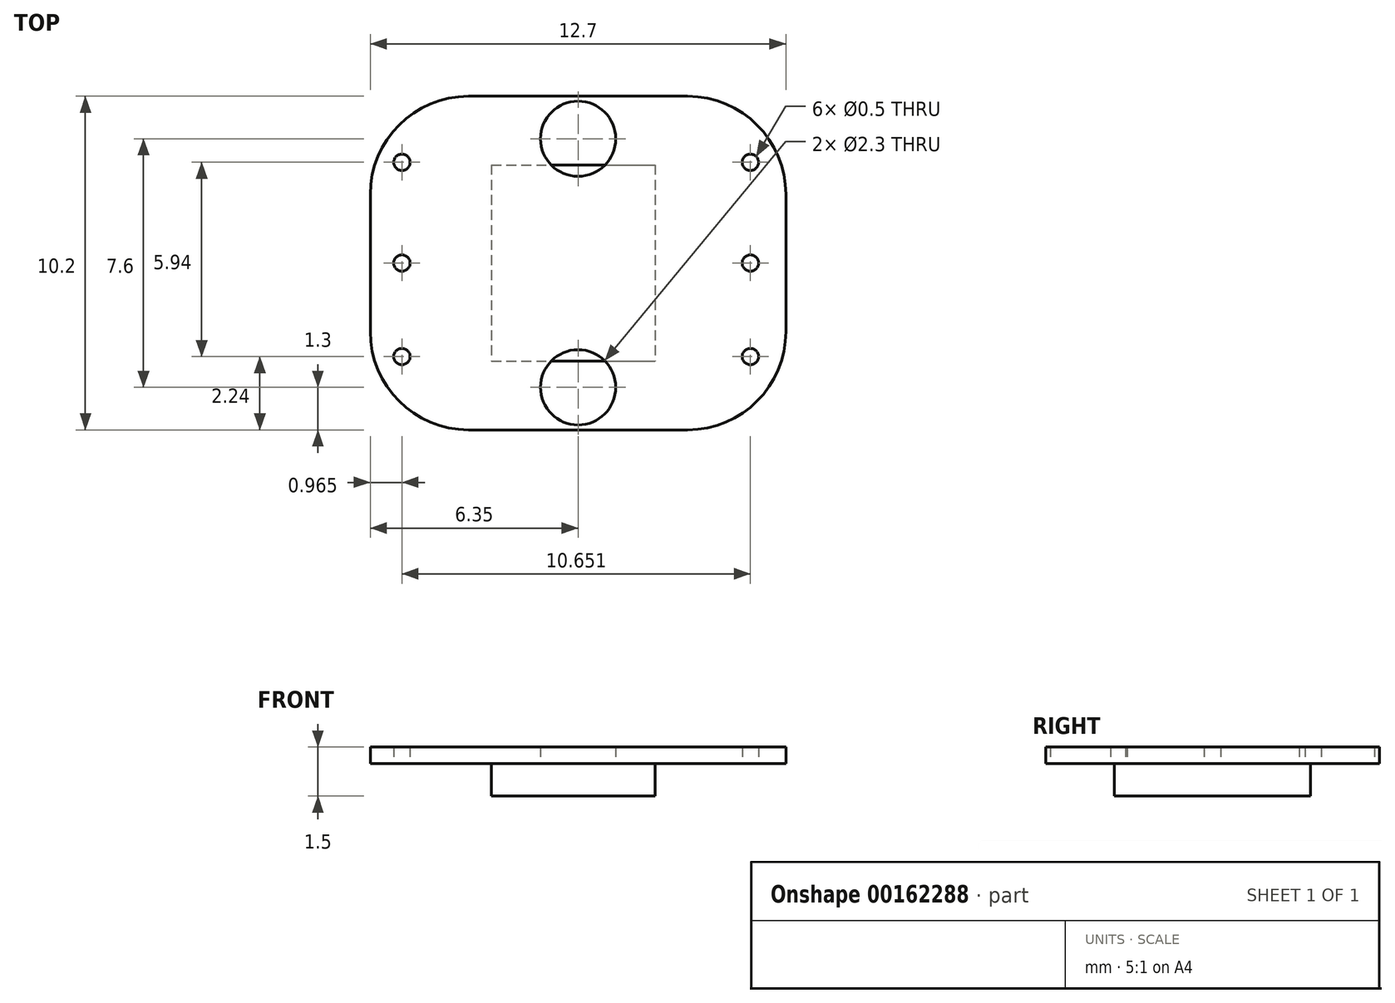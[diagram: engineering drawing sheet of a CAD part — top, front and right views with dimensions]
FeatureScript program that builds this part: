
annotation { "Feature Type Name" : "Feature", "Feature Type Description" : "" }
export const myFeature = defineFeature(function(context is Context, id is Id, definition is map)
    precondition{}
    {
        {
            var Q0;
            Q0=qCreatedBy(makeId("Top.planeOp"),FACE);
            var sketch = newSketch(context, id + "F0", { "sketchPlane" : qUnion([Q0])});
            skLineSegment(sketch, "E0.bottom", {"start": v(0, 10.2) * mm, "end": v(12.7, 10.2) * mm});
            skLineSegment(sketch, "E0.top", {"start": v(0, 0) * mm, "end": v(12.7, 0) * mm});
            skLineSegment(sketch, "E0.left", {"start": v(0, 10.2) * mm, "end": v(0, 0) * mm});
            skLineSegment(sketch, "E0.right", {"start": v(12.7, 10.2) * mm, "end": v(12.7, 0) * mm});
            skLineSegment(sketch, "E1.bottom", {"start": v(3.7, 8.1) * mm, "end": v(8.7, 8.1) * mm});
            skLineSegment(sketch, "E1.top", {"start": v(3.7, 2.1) * mm, "end": v(8.7, 2.1) * mm});
            skLineSegment(sketch, "E1.left", {"start": v(3.7, 8.1) * mm, "end": v(3.7, 2.1) * mm});
            skLineSegment(sketch, "E1.right", {"start": v(8.7, 8.1) * mm, "end": v(8.7, 2.1) * mm});
            skPoint(sketch, "E2", {"position": v(0.97, 5.1) * mm});
            skPoint(sketch, "E2.positionSnap0", {"position": v(0, 5.1) * mm});
            skPoint(sketch, "E3", {"position": v(0.97, 8.18) * mm});
            skPoint(sketch, "E4", {"position": v(0.97, 2.24) * mm});
            skPoint(sketch, "E5", {"position": v(11.62, 5.1) * mm});
            skPoint(sketch, "E5.positionSnap0", {"position": v(12.7, 5.1) * mm});
            skPoint(sketch, "E6", {"position": v(11.62, 8.18) * mm});
            skPoint(sketch, "E7", {"position": v(11.62, 2.24) * mm});
            skPoint(sketch, "E8", {"position": v(6.35, 8.9) * mm});
            skPoint(sketch, "E8.positionSnap0", {"position": v(6.35, 10.2) * mm});
            skPoint(sketch, "E9", {"position": v(6.35, 1.3) * mm});
            skPoint(sketch, "E9.positionSnap0", {"position": v(6.35, 0) * mm});
            skSolve(sketch);
        }
        {
            var Q0;
            Q0=makeQuery(id+"F0.imprint","IMPRINT",FACE,{"disambiguationData":[TD([[makeQuery(id+"F0.imprint","IMPRINT",EDGE,{"derivedFrom":sQuery(id+"F0.wireOp",EDGE,"E0.bottom")}),-1.0]])]});
            var Q1;
            Q1=makeQuery(id+"F0.imprint","IMPRINT",FACE,{"disambiguationData":[TD([[makeQuery(id+"F0.imprint","IMPRINT",EDGE,{"derivedFrom":sQuery(id+"F0.wireOp",EDGE,"E1.bottom")}),-1.0]])]});
            extrude(context, id + "F1", {"entities" : qUnion([Q0, Q1]), "depth" : 0.5 * mm});
        }
        {
            var Q0;
            Q0=makeQuery(id+"F0.imprint","IMPRINT",FACE,{"disambiguationData":[TD([[makeQuery(id+"F0.imprint","IMPRINT",EDGE,{"derivedFrom":sQuery(id+"F0.wireOp",EDGE,"E1.bottom")}),-1.0]])]});
            extrude(context, id + "F2", {"entities" : qUnion([Q0]), "oppositeDirection" : true, "depth" : 1 * mm});
        }
        {
            var Q0;
            Q0=sQuery(id+"F0.wireOp",VERTEX,"E7");
            var Q1;
            Q1=sQuery(id+"F0.wireOp",VERTEX,"E5");
            var Q2;
            Q2=sQuery(id+"F0.wireOp",VERTEX,"E6");
            var Q3;
            Q3=sQuery(id+"F0.wireOp",VERTEX,"E3");
            var Q4;
            Q4=sQuery(id+"F0.wireOp",VERTEX,"E2");
            var Q5;
            Q5=sQuery(id+"F0.wireOp",VERTEX,"E4");
            var Q6;
            Q6=makeQuery(id+"F1.opExtrude","SWEPT_BODY",BODY,{"disambiguationData":[OSD([sQuery(id+"F0.wireOp",EDGE,"E0.bottom"),sQuery(id+"F0.wireOp",EDGE,"E0.top"),sQuery(id+"F0.wireOp",EDGE,"E0.left"),sQuery(id+"F0.wireOp",EDGE,"E0.right")])]});
            hole(context, id + "F3", {"style" : HoleStyle.SIMPLE, "endStyle" : HoleEndStyle.THROUGH, "oppositeDirection" : true, "holeDiameter" : 0.5 * mm, "startFromSketch" : true, "locations" : qUnion([Q0, Q1, Q2, Q3, Q4, Q5]), "scope" : qUnion([Q6]), "isTappedThrough" : true});
        }
        {
            var Q0;
            Q0=sQuery(id+"F0.wireOp",VERTEX,"E9");
            var Q1;
            Q1=sQuery(id+"F0.wireOp",VERTEX,"E8");
            var Q2;
            Q2=makeQuery(id+"F1.opExtrude","SWEPT_BODY",BODY,{"disambiguationData":[OSD([sQuery(id+"F0.wireOp",EDGE,"E0.bottom"),sQuery(id+"F0.wireOp",EDGE,"E0.top"),sQuery(id+"F0.wireOp",EDGE,"E0.left"),sQuery(id+"F0.wireOp",EDGE,"E0.right")])]});
            hole(context, id + "F4", {"style" : HoleStyle.SIMPLE, "endStyle" : HoleEndStyle.THROUGH, "oppositeDirection" : true, "holeDiameter" : 2.3 * mm, "startFromSketch" : true, "locations" : qUnion([Q0, Q1]), "scope" : qUnion([Q2]), "isTappedThrough" : true});
        }
        {
            var Q0;
            Q0=makeQuery(id+"F1.opExtrude","SWEPT_EDGE",EDGE,{"disambiguationData":[OSD([sQuery(id+"F0.wireOp",EDGE,"E0.bottom"),sQuery(id+"F0.wireOp",EDGE,"E0.left")])]});
            var Q1;
            Q1=makeQuery(id+"F1.opExtrude","SWEPT_EDGE",EDGE,{"disambiguationData":[OSD([sQuery(id+"F0.wireOp",EDGE,"E0.bottom"),sQuery(id+"F0.wireOp",EDGE,"E0.right")])]});
            var Q2;
            Q2=makeQuery(id+"F1.opExtrude","SWEPT_EDGE",EDGE,{"disambiguationData":[OSD([sQuery(id+"F0.wireOp",EDGE,"E0.top"),sQuery(id+"F0.wireOp",EDGE,"E0.left")])]});
            var Q3;
            Q3=makeQuery(id+"F1.opExtrude","SWEPT_EDGE",EDGE,{"disambiguationData":[OSD([sQuery(id+"F0.wireOp",EDGE,"E0.top"),sQuery(id+"F0.wireOp",EDGE,"E0.right")])]});
            fillet(context, id + "F5", {"entities" : qUnion([Q0, Q1, Q2, Q3]), "radius" : 3 * mm, "allowEdgeOverflow" : false});
        }
    });
